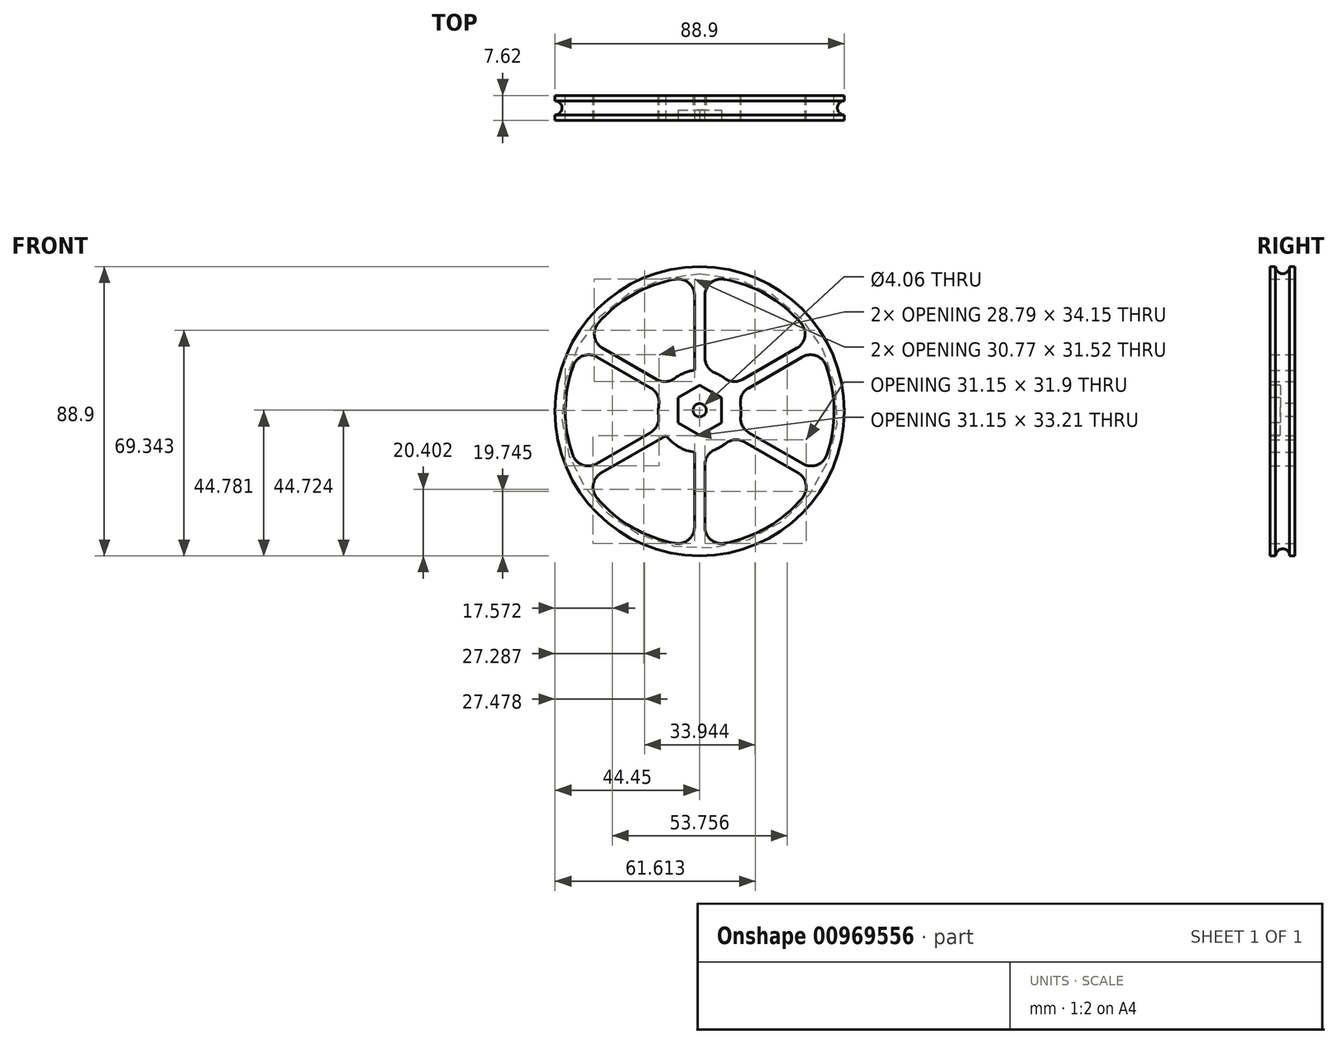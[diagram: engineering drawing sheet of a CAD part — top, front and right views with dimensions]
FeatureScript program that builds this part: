
annotation { "Feature Type Name" : "Feature", "Feature Type Description" : "" }
export const myFeature = defineFeature(function(context is Context, id is Id, definition is map)
    precondition{}
    {
        {
            var Q0;
            Q0=qCreatedBy(makeId("Top.planeOp"),FACE);
            var sketch = newSketch(context, id + "F0", { "sketchPlane" : qUnion([Q0])});
            skLineSegment(sketch, "E0", {"start": v(0, 0) * mm, "end": v(0, 3.81) * mm});
            skLineSegment(sketch, "E1", {"start": v(0, 0) * mm, "end": v(0, -3.81) * mm});
            skLineSegment(sketch, "E2", {"start": v(0, 3.81) * mm, "end": v(44.45, 3.81) * mm});
            skLineSegment(sketch, "E3", {"start": v(0, -3.81) * mm, "end": v(44.45, -3.81) * mm});
            skLineSegment(sketch, "E4", {"start": v(44.45, 3.8) * mm, "end": v(44.45, 2.16) * mm});
            skLineSegment(sketch, "E5", {"start": v(44.45, -3.8) * mm, "end": v(44.45, -2.16) * mm});
            skLineSegment(sketch, "E6", {"start": v(44.45, 2.16) * mm, "end": v(44.45, -2.16) * mm});
            skCircle(sketch, "E7", {"center": v(44.45, 0) * mm, "radius": 2.16 * mm});
            skLineSegment(sketch, "E8", {"start": v(44.45, 2.16) * mm, "end": v(0, 2.16) * mm});
            skLineSegment(sketch, "E9", {"start": v(44.45, -2.16) * mm, "end": v(0, -2.16) * mm});
            skPoint(sketch, "E9.endSnap0", {"position": v(0, -1.9) * mm});
            skSolve(sketch);
        }
        {
            var Q0;
            {var subQ0=sQuery(id+"F0.wireOp",EDGE,"E2");Q0=makeQuery(id+"F0.imprint","IMPRINT",FACE,{"disambiguationData":[TD([[makeQuery(id+"F0.imprint","IMPRINT",EDGE,{"derivedFrom":subQ0}),-1.0]])]});}
            var Q1;
            {var subQ0=sQuery(id+"F0.wireOp",EDGE,"E3");Q1=makeQuery(id+"F0.imprint","IMPRINT",FACE,{"disambiguationData":[TD([[makeQuery(id+"F0.imprint","IMPRINT",EDGE,{"derivedFrom":subQ0}),1.0]])]});}
            var Q2;
            {var subQ0=sQuery(id+"F0.wireOp",EDGE,"E8");Q2=makeQuery(id+"F0.imprint","IMPRINT",FACE,{"disambiguationData":[TD([[makeQuery(id+"F0.imprint","IMPRINT",EDGE,{"derivedFrom":subQ0}),1.0]])]});}
            var Q3;
            Q3 = qSketchRegion(id + "F2", true);
            var Q4;
            Q4=sQuery(id+"F0.wireOp",EDGE,"E1");
            revolve(context, id + "F1", {"surfaceOperationType" : NewSurfaceOperationType.NEW, "entities" : qUnion([Q0, Q1, Q2, Q3]), "axis" : qUnion([Q4]), "revolveType" : RevolveType.FULL});
        }
        {
            var Q0;
            Q0=makeQuery(id+"F1.opRevolve","SWEPT_FACE",FACE,{"disambiguationData":[OSD([sQuery(id+"F0.wireOp",EDGE,"E2")])]});
            var sketch = newSketch(context, id + "F2", { "sketchPlane" : qUnion([Q0])});
            skCircle(sketch, "E10", {"center": v(0, 0) * mm, "radius": 41.28 * mm});
            skSolve(sketch);
        }
        {
            var Q0;
            Q0=makeQuery(id+"F2.imprint","IMPRINT",FACE,{"disambiguationData":[TD([[makeQuery(id+"F2.imprint","IMPRINT",EDGE,{"derivedFrom":sQuery(id+"F2.wireOp",EDGE,"E10")}),1.0]])]});
            var Q1;
            Q1=sQuery(id+"F2.wireOp",EDGE,"E10");
            extrude(context, id + "F3", {"entities" : qUnion([Q0]), "operationType" : NewBodyOperationType.REMOVE, "surfaceEntities" : qUnion([Q1]), "endBound" : BoundingType.THROUGH_ALL, "oppositeDirection" : true, "depth" : 25.4 * mm, "offsetDistance" : 25.4 * mm});
        }
        {
            var Q0;
            Q0=qCreatedBy(makeId("Front.planeOp"),FACE);
            var sketch = newSketch(context, id + "F4", { "sketchPlane" : qUnion([Q0])});
            skLineSegment(sketch, "E11.0", {"start": v(-6.64, 4.17) * mm, "end": v(0, 8) * mm});
            skLineSegment(sketch, "E11.1", {"start": v(0, 8) * mm, "end": v(6.64, 4.17) * mm});
            skLineSegment(sketch, "E11.2", {"start": v(6.64, 4.17) * mm, "end": v(6.64, -3.5) * mm});
            skLineSegment(sketch, "E11.3", {"start": v(6.64, -3.5) * mm, "end": v(0, -7.34) * mm});
            skLineSegment(sketch, "E11.4", {"start": v(0, -7.34) * mm, "end": v(-6.64, -3.5) * mm});
            skLineSegment(sketch, "E11.5", {"start": v(-6.64, -3.5) * mm, "end": v(-6.64, 4.17) * mm});
            skCircle(sketch, "E12", {"center": v(0, 0) * mm, "radius": 12.7 * mm});
            skLineSegment(sketch, "E13", {"start": v(0, 8) * mm, "end": v(0, 9.82) * mm});
            skLineSegment(sketch, "E14", {"start": v(0, 9.82) * mm, "end": v(0, -7.34) * mm});
            skCircle(sketch, "E15", {"center": v(0, 0) * mm, "radius": 9.82 * mm});
            skLineSegment(sketch, "E16", {"start": v(0, -7.34) * mm, "end": v(0, 8) * mm});
            skLineSegment(sketch, "E17", {"start": v(6.64, 4.17) * mm, "end": v(-6.64, -3.5) * mm});
            skLineSegment(sketch, "E18", {"start": v(6.64, -3.5) * mm, "end": v(8.64, -4.66) * mm});
            skLineSegment(sketch, "E19", {"start": v(6.64, -3.5) * mm, "end": v(-6.64, 4.17) * mm});
            skLineSegment(sketch, "E20", {"start": v(0, 8) * mm, "end": v(0, 41.58) * mm});
            skCircle(sketch, "E21", {"center": v(0, 0) * mm, "radius": 41.58 * mm});
            skLineSegment(sketch, "E22", {"start": v(6.64, 4.17) * mm, "end": v(35.87, 21.04) * mm});
            skLineSegment(sketch, "E23", {"start": v(8.64, -4.66) * mm, "end": v(36.16, -20.54) * mm});
            skLineSegment(sketch, "E24", {"start": v(0, -7.34) * mm, "end": v(0, -41.58) * mm});
            skLineSegment(sketch, "E25", {"start": v(-6.64, -3.5) * mm, "end": v(-36.16, -20.54) * mm});
            skLineSegment(sketch, "E26", {"start": v(-6.64, 4.17) * mm, "end": v(-35.87, 21.04) * mm});
            skLineSegment(sketch, "E27", {"start": v(1.59, 12.6) * mm, "end": v(1.59, 41.55) * mm});
            skLineSegment(sketch, "E28", {"start": v(-1.59, 12.6) * mm, "end": v(-1.59, 41.55) * mm});
            skLineSegment(sketch, "E29", {"start": v(-9.94, 7.9) * mm, "end": v(-35.04, 22.4) * mm});
            skLineSegment(sketch, "E30", {"start": v(-11.6, 5.19) * mm, "end": v(-36.65, 19.66) * mm});
            skLineSegment(sketch, "E31", {"start": v(-11.82, -4.66) * mm, "end": v(-36.91, -19.15) * mm});
            skLineSegment(sketch, "E32", {"start": v(-10.3, -7.44) * mm, "end": v(-35.34, -21.9) * mm});
            skLineSegment(sketch, "E33", {"start": v(10.3, -7.44) * mm, "end": v(35.34, -21.9) * mm});
            skLineSegment(sketch, "E34", {"start": v(11.82, -4.66) * mm, "end": v(36.91, -19.15) * mm});
            skLineSegment(sketch, "E35", {"start": v(11.6, 5.19) * mm, "end": v(36.65, 19.66) * mm});
            skLineSegment(sketch, "E36", {"start": v(9.94, 7.9) * mm, "end": v(35.04, 22.4) * mm});
            skLineSegment(sketch, "E37", {"start": v(1.59, -12.6) * mm, "end": v(1.59, -41.55) * mm});
            skPoint(sketch, "E37.startSnap0", {"position": v(22.4, -12.6) * mm});
            skLineSegment(sketch, "E38", {"start": v(-1.59, -12.6) * mm, "end": v(-1.59, -41.55) * mm});
            skSolve(sketch);
        }
        {
            var Q0;
            {var subQ0=sQuery(id+"F4.wireOp",EDGE,"E36");Q0=makeQuery(id+"F4.imprint","IMPRINT",FACE,{"disambiguationData":[TD([[makeQuery(id+"F4.imprint","IMPRINT",EDGE,{"derivedFrom":subQ0}),-1.0]])]});}
            var Q1;
            {var subQ0=sQuery(id+"F4.wireOp",EDGE,"E35");Q1=makeQuery(id+"F4.imprint","IMPRINT",FACE,{"disambiguationData":[TD([[makeQuery(id+"F4.imprint","IMPRINT",EDGE,{"derivedFrom":subQ0}),1.0]])]});}
            var Q2;
            {var subQ0=sQuery(id+"F4.wireOp",EDGE,"E27");Q2=makeQuery(id+"F4.imprint","IMPRINT",FACE,{"disambiguationData":[TD([[makeQuery(id+"F4.imprint","IMPRINT",EDGE,{"derivedFrom":subQ0}),1.0]])]});}
            var Q3;
            {var subQ0=sQuery(id+"F4.wireOp",EDGE,"E28");Q3=makeQuery(id+"F4.imprint","IMPRINT",FACE,{"disambiguationData":[TD([[makeQuery(id+"F4.imprint","IMPRINT",EDGE,{"derivedFrom":subQ0}),-1.0]])]});}
            var Q4;
            {var subQ0=sQuery(id+"F4.wireOp",EDGE,"E29");Q4=makeQuery(id+"F4.imprint","IMPRINT",FACE,{"disambiguationData":[TD([[makeQuery(id+"F4.imprint","IMPRINT",EDGE,{"derivedFrom":subQ0}),1.0]])]});}
            var Q5;
            {var subQ0=sQuery(id+"F4.wireOp",EDGE,"E30");Q5=makeQuery(id+"F4.imprint","IMPRINT",FACE,{"disambiguationData":[TD([[makeQuery(id+"F4.imprint","IMPRINT",EDGE,{"derivedFrom":subQ0}),-1.0]])]});}
            var Q6;
            {var subQ0=sQuery(id+"F4.wireOp",EDGE,"E31");Q6=makeQuery(id+"F4.imprint","IMPRINT",FACE,{"disambiguationData":[TD([[makeQuery(id+"F4.imprint","IMPRINT",EDGE,{"derivedFrom":subQ0}),1.0]])]});}
            var Q7;
            {var subQ0=sQuery(id+"F4.wireOp",EDGE,"E32");Q7=makeQuery(id+"F4.imprint","IMPRINT",FACE,{"disambiguationData":[TD([[makeQuery(id+"F4.imprint","IMPRINT",EDGE,{"derivedFrom":subQ0}),-1.0]])]});}
            var Q8;
            {var subQ0=sQuery(id+"F4.wireOp",EDGE,"E33");Q8=makeQuery(id+"F4.imprint","IMPRINT",FACE,{"disambiguationData":[TD([[makeQuery(id+"F4.imprint","IMPRINT",EDGE,{"derivedFrom":subQ0}),1.0]])]});}
            var Q9;
            {var subQ0=sQuery(id+"F4.wireOp",EDGE,"E34");Q9=makeQuery(id+"F4.imprint","IMPRINT",FACE,{"disambiguationData":[TD([[makeQuery(id+"F4.imprint","IMPRINT",EDGE,{"derivedFrom":subQ0}),-1.0]])]});}
            var Q10;
            {var subQ0=sQuery(id+"F4.wireOp",EDGE,"E37");Q10=makeQuery(id+"F4.imprint","IMPRINT",FACE,{"disambiguationData":[TD([[makeQuery(id+"F4.imprint","IMPRINT",EDGE,{"derivedFrom":subQ0}),-1.0]])]});}
            var Q11;
            {var subQ0=sQuery(id+"F4.wireOp",EDGE,"E38");Q11=makeQuery(id+"F4.imprint","IMPRINT",FACE,{"disambiguationData":[TD([[makeQuery(id+"F4.imprint","IMPRINT",EDGE,{"derivedFrom":subQ0}),1.0]])]});}
            extrude(context, id + "F5", {"entities" : qUnion([Q0, Q1, Q2, Q3, Q4, Q5, Q6, Q7, Q8, Q9, Q10, Q11]), "operationType" : NewBodyOperationType.ADD, "endBound" : BoundingType.SYMMETRIC, "depth" : 7.62 * mm, "offsetDistance" : 25.4 * mm});
        }
        {
            var Q0;
            {var subQ5=sQuery(id+"F4.wireOp",EDGE,"E12");var subQ7=makeQuery(id+"F4.imprint","INTERSECT",VERTEX,{"derivedFrom":[subQ5,sQuery(id+"F4.wireOp",EDGE,"E35")]});Q0=makeQuery(id+"F4.imprint","IMPRINT",FACE,{"disambiguationData":[TD([[makeQuery(id+"F4.imprint","IMPRINT",EDGE,{"disambiguationData":[TD([[subQ7,-1.0]])],"derivedFrom":subQ5}),1.0]])]});}
            var Q1;
            {var subQ0=sQuery(id+"F4.wireOp",EDGE,"E12");var subQ4=makeQuery(id+"F4.imprint","INTERSECT",VERTEX,{"derivedFrom":[subQ0,sQuery(id+"F4.wireOp",EDGE,"E36")]});Q1=makeQuery(id+"F4.imprint","IMPRINT",FACE,{"disambiguationData":[TD([[makeQuery(id+"F4.imprint","IMPRINT",EDGE,{"disambiguationData":[TD([[subQ4,1.0]])],"derivedFrom":subQ0}),1.0]])]});}
            var Q2;
            {var subQ4=sQuery(id+"F4.wireOp",EDGE,"E12");var subQ8=makeQuery(id+"F4.imprint","INTERSECT",VERTEX,{"derivedFrom":[subQ4,sQuery(id+"F4.wireOp",EDGE,"E28")]});Q2=makeQuery(id+"F4.imprint","IMPRINT",FACE,{"disambiguationData":[TD([[makeQuery(id+"F4.imprint","IMPRINT",EDGE,{"disambiguationData":[TD([[subQ8,1.0]])],"derivedFrom":subQ4}),1.0]])]});}
            var Q3;
            {var subQ5=sQuery(id+"F4.wireOp",EDGE,"E12");var subQ8=makeQuery(id+"F4.imprint","INTERSECT",VERTEX,{"derivedFrom":[subQ5,sQuery(id+"F4.wireOp",EDGE,"E30")]});Q3=makeQuery(id+"F4.imprint","IMPRINT",FACE,{"disambiguationData":[TD([[makeQuery(id+"F4.imprint","IMPRINT",EDGE,{"disambiguationData":[TD([[subQ8,1.0]])],"derivedFrom":subQ5}),1.0]])]});}
            var Q4;
            {var subQ0=sQuery(id+"F4.wireOp",EDGE,"E12");var subQ9=makeQuery(id+"F4.imprint","INTERSECT",VERTEX,{"derivedFrom":[subQ0,sQuery(id+"F4.wireOp",EDGE,"E32")]});Q4=makeQuery(id+"F4.imprint","IMPRINT",FACE,{"disambiguationData":[TD([[makeQuery(id+"F4.imprint","IMPRINT",EDGE,{"disambiguationData":[TD([[subQ9,1.0]])],"derivedFrom":subQ0}),1.0]])]});}
            var Q5;
            {var subQ0=sQuery(id+"F4.wireOp",EDGE,"E12");var subQ4=makeQuery(id+"F4.imprint","INTERSECT",VERTEX,{"derivedFrom":[subQ0,sQuery(id+"F4.wireOp",EDGE,"E37")]});Q5=makeQuery(id+"F4.imprint","IMPRINT",FACE,{"disambiguationData":[TD([[makeQuery(id+"F4.imprint","IMPRINT",EDGE,{"disambiguationData":[TD([[subQ4,1.0]])],"derivedFrom":subQ0}),1.0]])]});}
            var Q6;
            {var subQ0=sQuery(id+"F4.wireOp",EDGE,"E11.2");Q6=makeQuery(id+"F4.imprint","IMPRINT",FACE,{"disambiguationData":[TD([[makeQuery(id+"F4.imprint","IMPRINT",EDGE,{"derivedFrom":subQ0}),1.0]])]});}
            var Q7;
            {var subQ0=sQuery(id+"F4.wireOp",EDGE,"E11.3");Q7=makeQuery(id+"F4.imprint","IMPRINT",FACE,{"disambiguationData":[TD([[makeQuery(id+"F4.imprint","IMPRINT",EDGE,{"derivedFrom":subQ0}),1.0]])]});}
            var Q8;
            {var subQ0=sQuery(id+"F4.wireOp",EDGE,"E11.4");Q8=makeQuery(id+"F4.imprint","IMPRINT",FACE,{"disambiguationData":[TD([[makeQuery(id+"F4.imprint","IMPRINT",EDGE,{"derivedFrom":subQ0}),1.0]])]});}
            var Q9;
            {var subQ0=sQuery(id+"F4.wireOp",EDGE,"E11.5");Q9=makeQuery(id+"F4.imprint","IMPRINT",FACE,{"disambiguationData":[TD([[makeQuery(id+"F4.imprint","IMPRINT",EDGE,{"derivedFrom":subQ0}),1.0]])]});}
            var Q10;
            {var subQ0=sQuery(id+"F4.wireOp",EDGE,"E11.0");Q10=makeQuery(id+"F4.imprint","IMPRINT",FACE,{"disambiguationData":[TD([[makeQuery(id+"F4.imprint","IMPRINT",EDGE,{"derivedFrom":subQ0}),1.0]])]});}
            var Q11;
            {var subQ0=sQuery(id+"F4.wireOp",EDGE,"F7P9rnZc-xmLm-aryr-64I1-wp8JT27DvNvk");Q11=makeQuery(id+"F4.imprint","IMPRINT",FACE,{"disambiguationData":[TD([[makeQuery(id+"F4.imprint","IMPRINT",EDGE,{"derivedFrom":subQ0}),1.0]])]});}
            var Q12;
            {var subQ0=sQuery(id+"F4.wireOp",EDGE,"E11.1");Q12=makeQuery(id+"F4.imprint","IMPRINT",FACE,{"disambiguationData":[TD([[makeQuery(id+"F4.imprint","IMPRINT",EDGE,{"derivedFrom":subQ0}),1.0]])]});}
            extrude(context, id + "F6", {"entities" : qUnion([Q0, Q1, Q2, Q3, Q4, Q5, Q6, Q7, Q8, Q9, Q10, Q11, Q12]), "operationType" : NewBodyOperationType.ADD, "endBound" : BoundingType.SYMMETRIC, "depth" : 7.62 * mm, "offsetDistance" : 25.4 * mm});
        }
        {
            var Q0;
            {var subQ0=sQuery(id+"F4.wireOp",EDGE,"E11.4");Q0=makeQuery(id+"F4.imprint","IMPRINT",FACE,{"disambiguationData":[TD([[makeQuery(id+"F4.imprint","IMPRINT",EDGE,{"derivedFrom":subQ0}),-1.0]])]});}
            var Q1;
            {var subQ0=sQuery(id+"F4.wireOp",EDGE,"E11.5");Q1=makeQuery(id+"F4.imprint","IMPRINT",FACE,{"disambiguationData":[TD([[makeQuery(id+"F4.imprint","IMPRINT",EDGE,{"derivedFrom":subQ0}),-1.0]])]});}
            var Q2;
            {var subQ0=sQuery(id+"F4.wireOp",EDGE,"E11.0");Q2=makeQuery(id+"F4.imprint","IMPRINT",FACE,{"disambiguationData":[TD([[makeQuery(id+"F4.imprint","IMPRINT",EDGE,{"derivedFrom":subQ0}),-1.0]])]});}
            var Q3;
            {var subQ0=sQuery(id+"F4.wireOp",EDGE,"E11.1");Q3=makeQuery(id+"F4.imprint","IMPRINT",FACE,{"disambiguationData":[TD([[makeQuery(id+"F4.imprint","IMPRINT",EDGE,{"derivedFrom":subQ0}),-1.0]])]});}
            var Q4;
            {var subQ0=sQuery(id+"F4.wireOp",EDGE,"E11.2");Q4=makeQuery(id+"F4.imprint","IMPRINT",FACE,{"disambiguationData":[TD([[makeQuery(id+"F4.imprint","IMPRINT",EDGE,{"derivedFrom":subQ0}),-1.0]])]});}
            var Q5;
            {var subQ0=sQuery(id+"F4.wireOp",EDGE,"E11.3");Q5=makeQuery(id+"F4.imprint","IMPRINT",FACE,{"disambiguationData":[TD([[makeQuery(id+"F4.imprint","IMPRINT",EDGE,{"derivedFrom":subQ0}),-1.0]])]});}
            var Q6;
            Q6 = qSketchRegion(id + "F8", true);
            extrude(context, id + "F7", {"entities" : qUnion([Q0, Q1, Q2, Q3, Q4, Q5, Q6]), "operationType" : NewBodyOperationType.ADD, "endBound" : BoundingType.SYMMETRIC, "depth" : 7.62 * mm, "offsetDistance" : 25.4 * mm});
        }
        {
            var Q0;
            {var subQ0=sQuery(id+"F4.wireOp",EDGE,"E11.5");var subQ1=sQuery(id+"F4.wireOp",EDGE,"E11.4");var subQ2=sQuery(id+"F4.wireOp",EDGE,"E11.3");var subQ3=sQuery(id+"F4.wireOp",EDGE,"E11.2");var subQ4=sQuery(id+"F4.wireOp",EDGE,"E11.1");var subQ5=sQuery(id+"F4.wireOp",EDGE,"E11.0");Q0=makeQuery(id+"F7.boolean.opBoolean","MERGE",FACE,{"derivedFrom":[makeQuery(id+"F6.opExtrude","CAP_FACE",FACE,{"disambiguationData":[OSD([subQ5,subQ4,subQ3,subQ2,subQ1,subQ0,sQuery(id+"F4.wireOp",EDGE,"E12")])],"isStart":false}),makeQuery(id+"F7.opExtrude","CAP_FACE",FACE,{"disambiguationData":[OSD([subQ5,subQ4,subQ3,subQ2,subQ1,subQ0])],"isStart":false})]});}
            var sketch = newSketch(context, id + "F8", { "sketchPlane" : qUnion([Q0])});
            skLineSegment(sketch, "E39.1", {"start": v(-6.64, 4.17) * mm, "end": v(0, 8) * mm});
            skLineSegment(sketch, "E39.2", {"start": v(0, -7.34) * mm, "end": v(0, 8) * mm});
            skLineSegment(sketch, "E39.3", {"start": v(0, 8) * mm, "end": v(6.64, 4.17) * mm});
            skLineSegment(sketch, "E39.4", {"start": v(6.64, -3.5) * mm, "end": v(-6.64, 4.17) * mm});
            skLineSegment(sketch, "E39.5", {"start": v(-6.64, -3.5) * mm, "end": v(-6.64, 4.17) * mm});
            skLineSegment(sketch, "E39.6", {"start": v(0, -7.34) * mm, "end": v(-6.64, -3.5) * mm});
            skLineSegment(sketch, "E39.7", {"start": v(6.64, 4.17) * mm, "end": v(-6.64, -3.5) * mm});
            skLineSegment(sketch, "E39.8", {"start": v(6.64, 4.17) * mm, "end": v(6.64, -3.5) * mm});
            skLineSegment(sketch, "E39.9", {"start": v(6.64, -3.5) * mm, "end": v(0, -7.34) * mm});
            skPoint(sketch, "E39.10", {"position": v(6.64, 0.33) * mm});
            skCircle(sketch, "E40", {"center": v(9.99, -16.46) * mm, "radius": 1.14 * mm});
            skCircle(sketch, "E41", {"center": v(0, 0.33) * mm, "radius": 2.03 * mm});
            skSolve(sketch);
        }
        {
            var Q0;
            {var subQ0=sQuery(id+"F8.wireOp",EDGE,"E39.8");Q0=makeQuery(id+"F8.imprint","IMPRINT",FACE,{"disambiguationData":[TD([[makeQuery(id+"F8.imprint","IMPRINT",EDGE,{"derivedFrom":subQ0}),-1.0]])]});}
            var Q1;
            {var subQ0=sQuery(id+"F8.wireOp",EDGE,"E39.9");Q1=makeQuery(id+"F8.imprint","IMPRINT",FACE,{"disambiguationData":[TD([[makeQuery(id+"F8.imprint","IMPRINT",EDGE,{"derivedFrom":subQ0}),-1.0]])]});}
            var Q2;
            {var subQ0=sQuery(id+"F8.wireOp",EDGE,"E39.6");Q2=makeQuery(id+"F8.imprint","IMPRINT",FACE,{"disambiguationData":[TD([[makeQuery(id+"F8.imprint","IMPRINT",EDGE,{"derivedFrom":subQ0}),-1.0]])]});}
            var Q3;
            {var subQ0=sQuery(id+"F8.wireOp",EDGE,"E39.5");Q3=makeQuery(id+"F8.imprint","IMPRINT",FACE,{"disambiguationData":[TD([[makeQuery(id+"F8.imprint","IMPRINT",EDGE,{"derivedFrom":subQ0}),-1.0]])]});}
            var Q4;
            {var subQ0=sQuery(id+"F8.wireOp",EDGE,"E39.1");Q4=makeQuery(id+"F8.imprint","IMPRINT",FACE,{"disambiguationData":[TD([[makeQuery(id+"F8.imprint","IMPRINT",EDGE,{"derivedFrom":subQ0}),-1.0]])]});}
            var Q5;
            {var subQ0=sQuery(id+"F8.wireOp",EDGE,"E39.3");Q5=makeQuery(id+"F8.imprint","IMPRINT",FACE,{"disambiguationData":[TD([[makeQuery(id+"F8.imprint","IMPRINT",EDGE,{"derivedFrom":subQ0}),-1.0]])]});}
            extrude(context, id + "F9", {"entities" : qUnion([Q0, Q1, Q2, Q3, Q4, Q5]), "operationType" : NewBodyOperationType.REMOVE, "oppositeDirection" : true, "depth" : 3.17 * mm, "offsetDistance" : 25.4 * mm});
        }
        {
            var Q0;
            {var subQ0=sQuery(id+"F8.wireOp",EDGE,"E41");var subQ1=sQuery(id+"F8.wireOp",EDGE,"E39.2");var subQ2=makeQuery(id+"F8.imprint","INTERSECT",VERTEX,{"disambiguationData":[OD(0.0)],"derivedFrom":[subQ1,subQ0]});Q0=makeQuery(id+"F8.imprint","IMPRINT",FACE,{"disambiguationData":[TD([[makeQuery(id+"F8.imprint","IMPRINT",EDGE,{"disambiguationData":[TD([[subQ2,1.0]])],"derivedFrom":subQ0}),1.0]])]});}
            var Q1;
            {var subQ0=sQuery(id+"F8.wireOp",EDGE,"E41");var subQ1=sQuery(id+"F8.wireOp",EDGE,"E39.4");var subQ2=makeQuery(id+"F8.imprint","INTERSECT",VERTEX,{"disambiguationData":[OD(1.0)],"derivedFrom":[subQ1,subQ0]});Q1=makeQuery(id+"F8.imprint","IMPRINT",FACE,{"disambiguationData":[TD([[makeQuery(id+"F8.imprint","IMPRINT",EDGE,{"disambiguationData":[TD([[subQ2,-1.0]])],"derivedFrom":subQ0}),1.0]])]});}
            var Q2;
            {var subQ0=sQuery(id+"F8.wireOp",EDGE,"E41");var subQ1=sQuery(id+"F8.wireOp",EDGE,"E39.2");var subQ2=makeQuery(id+"F8.imprint","INTERSECT",VERTEX,{"disambiguationData":[OD(1.0)],"derivedFrom":[subQ1,subQ0]});Q2=makeQuery(id+"F8.imprint","IMPRINT",FACE,{"disambiguationData":[TD([[makeQuery(id+"F8.imprint","IMPRINT",EDGE,{"disambiguationData":[TD([[subQ2,-1.0]])],"derivedFrom":subQ0}),1.0]])]});}
            var Q3;
            {var subQ0=sQuery(id+"F8.wireOp",EDGE,"E41");var subQ1=sQuery(id+"F8.wireOp",EDGE,"E39.2");var subQ2=makeQuery(id+"F8.imprint","INTERSECT",VERTEX,{"disambiguationData":[OD(1.0)],"derivedFrom":[subQ1,subQ0]});Q3=makeQuery(id+"F8.imprint","IMPRINT",FACE,{"disambiguationData":[TD([[makeQuery(id+"F8.imprint","IMPRINT",EDGE,{"disambiguationData":[TD([[subQ2,1.0]])],"derivedFrom":subQ0}),1.0]])]});}
            var Q4;
            {var subQ0=sQuery(id+"F8.wireOp",EDGE,"E41");var subQ1=sQuery(id+"F8.wireOp",EDGE,"E39.4");var subQ2=makeQuery(id+"F8.imprint","INTERSECT",VERTEX,{"disambiguationData":[OD(0.0)],"derivedFrom":[subQ1,subQ0]});Q4=makeQuery(id+"F8.imprint","IMPRINT",FACE,{"disambiguationData":[TD([[makeQuery(id+"F8.imprint","IMPRINT",EDGE,{"disambiguationData":[TD([[subQ2,-1.0]])],"derivedFrom":subQ0}),1.0]])]});}
            var Q5;
            {var subQ0=sQuery(id+"F8.wireOp",EDGE,"E41");var subQ1=sQuery(id+"F8.wireOp",EDGE,"E39.2");var subQ2=makeQuery(id+"F8.imprint","INTERSECT",VERTEX,{"disambiguationData":[OD(0.0)],"derivedFrom":[subQ1,subQ0]});Q5=makeQuery(id+"F8.imprint","IMPRINT",FACE,{"disambiguationData":[TD([[makeQuery(id+"F8.imprint","IMPRINT",EDGE,{"disambiguationData":[TD([[subQ2,-1.0]])],"derivedFrom":subQ0}),1.0]])]});}
            extrude(context, id + "F10", {"entities" : qUnion([Q0, Q1, Q2, Q3, Q4, Q5]), "operationType" : NewBodyOperationType.REMOVE, "endBound" : BoundingType.THROUGH_ALL, "oppositeDirection" : true, "depth" : 25.4 * mm, "offsetDistance" : 25.4 * mm});
        }
        {
            var Q0;
            Q0=makeQuery(id+"F5.boolean.opBoolean","INTERSECT",EDGE,{"derivedFrom":[makeQuery(id+"F3.boolean.opBoolean","COPY",FACE,{"derivedFrom":makeQuery(id+"F3.opExtrude","SWEPT_FACE",FACE,{"disambiguationData":[OSD([sQuery(id+"F2.wireOp",EDGE,"E10")])]})}),makeQuery(id+"F5.opExtrude","CAP_FACE",FACE,{"disambiguationData":[OSD([sQuery(id+"F4.wireOp",EDGE,"E12"),sQuery(id+"F4.wireOp",EDGE,"E21"),sQuery(id+"F4.wireOp",EDGE,"E37"),sQuery(id+"F4.wireOp",EDGE,"E38")])],"isStart":false})]});
            var Q1;
            Q1=makeQuery(id+"F5.boolean.opBoolean","INTERSECT",EDGE,{"derivedFrom":[makeQuery(id+"F3.boolean.opBoolean","COPY",FACE,{"derivedFrom":makeQuery(id+"F3.opExtrude","SWEPT_FACE",FACE,{"disambiguationData":[OSD([sQuery(id+"F2.wireOp",EDGE,"E10")])]})}),makeQuery(id+"F5.opExtrude","SWEPT_FACE",FACE,{"disambiguationData":[OSD([sQuery(id+"F4.wireOp",EDGE,"E37")])]})]});
            var Q2;
            Q2=makeQuery(id+"F5.boolean.opBoolean","INTERSECT",EDGE,{"derivedFrom":[makeQuery(id+"F3.boolean.opBoolean","COPY",FACE,{"derivedFrom":makeQuery(id+"F3.opExtrude","SWEPT_FACE",FACE,{"disambiguationData":[OSD([sQuery(id+"F2.wireOp",EDGE,"E10")])]})}),makeQuery(id+"F5.opExtrude","SWEPT_FACE",FACE,{"disambiguationData":[OSD([sQuery(id+"F4.wireOp",EDGE,"E38")])]})]});
            var Q3;
            Q3=makeQuery(id+"F5.boolean.opBoolean","INTERSECT",EDGE,{"derivedFrom":[makeQuery(id+"F3.boolean.opBoolean","COPY",FACE,{"derivedFrom":makeQuery(id+"F3.opExtrude","SWEPT_FACE",FACE,{"disambiguationData":[OSD([sQuery(id+"F2.wireOp",EDGE,"E10")])]})}),makeQuery(id+"F5.opExtrude","SWEPT_FACE",FACE,{"disambiguationData":[OSD([sQuery(id+"F4.wireOp",EDGE,"E34")])]})]});
            var Q4;
            Q4=makeQuery(id+"F5.boolean.opBoolean","INTERSECT",EDGE,{"derivedFrom":[makeQuery(id+"F3.boolean.opBoolean","COPY",FACE,{"derivedFrom":makeQuery(id+"F3.opExtrude","SWEPT_FACE",FACE,{"disambiguationData":[OSD([sQuery(id+"F2.wireOp",EDGE,"E10")])]})}),makeQuery(id+"F5.opExtrude","CAP_FACE",FACE,{"disambiguationData":[OSD([sQuery(id+"F4.wireOp",EDGE,"E12"),sQuery(id+"F4.wireOp",EDGE,"E21"),sQuery(id+"F4.wireOp",EDGE,"E33"),sQuery(id+"F4.wireOp",EDGE,"E34")])],"isStart":false})]});
            var Q5;
            Q5=makeQuery(id+"F5.boolean.opBoolean","INTERSECT",EDGE,{"derivedFrom":[makeQuery(id+"F3.boolean.opBoolean","COPY",FACE,{"derivedFrom":makeQuery(id+"F3.opExtrude","SWEPT_FACE",FACE,{"disambiguationData":[OSD([sQuery(id+"F2.wireOp",EDGE,"E10")])]})}),makeQuery(id+"F5.opExtrude","CAP_FACE",FACE,{"disambiguationData":[OSD([sQuery(id+"F4.wireOp",EDGE,"E12"),sQuery(id+"F4.wireOp",EDGE,"E21"),sQuery(id+"F4.wireOp",EDGE,"E37"),sQuery(id+"F4.wireOp",EDGE,"E38")])],"isStart":true})]});
            var Q6;
            Q6=makeQuery(id+"F5.boolean.opBoolean","INTERSECT",EDGE,{"derivedFrom":[makeQuery(id+"F3.boolean.opBoolean","COPY",FACE,{"derivedFrom":makeQuery(id+"F3.opExtrude","SWEPT_FACE",FACE,{"disambiguationData":[OSD([sQuery(id+"F2.wireOp",EDGE,"E10")])]})}),makeQuery(id+"F5.opExtrude","CAP_FACE",FACE,{"disambiguationData":[OSD([sQuery(id+"F4.wireOp",EDGE,"E12"),sQuery(id+"F4.wireOp",EDGE,"E21"),sQuery(id+"F4.wireOp",EDGE,"E33"),sQuery(id+"F4.wireOp",EDGE,"E34")])],"isStart":true})]});
            var Q7;
            Q7=makeQuery(id+"F5.boolean.opBoolean","INTERSECT",EDGE,{"derivedFrom":[makeQuery(id+"F3.boolean.opBoolean","COPY",FACE,{"derivedFrom":makeQuery(id+"F3.opExtrude","SWEPT_FACE",FACE,{"disambiguationData":[OSD([sQuery(id+"F2.wireOp",EDGE,"E10")])]})}),makeQuery(id+"F5.opExtrude","SWEPT_FACE",FACE,{"disambiguationData":[OSD([sQuery(id+"F4.wireOp",EDGE,"E33")])]})]});
            var Q8;
            Q8=makeQuery(id+"F5.boolean.opBoolean","INTERSECT",EDGE,{"derivedFrom":[makeQuery(id+"F3.boolean.opBoolean","COPY",FACE,{"derivedFrom":makeQuery(id+"F3.opExtrude","SWEPT_FACE",FACE,{"disambiguationData":[OSD([sQuery(id+"F2.wireOp",EDGE,"E10")])]})}),makeQuery(id+"F5.opExtrude","CAP_FACE",FACE,{"disambiguationData":[OSD([sQuery(id+"F4.wireOp",EDGE,"E12"),sQuery(id+"F4.wireOp",EDGE,"E21"),sQuery(id+"F4.wireOp",EDGE,"E35"),sQuery(id+"F4.wireOp",EDGE,"E36")])],"isStart":true})]});
            var Q9;
            Q9=makeQuery(id+"F5.boolean.opBoolean","INTERSECT",EDGE,{"derivedFrom":[makeQuery(id+"F3.boolean.opBoolean","COPY",FACE,{"derivedFrom":makeQuery(id+"F3.opExtrude","SWEPT_FACE",FACE,{"disambiguationData":[OSD([sQuery(id+"F2.wireOp",EDGE,"E10")])]})}),makeQuery(id+"F5.opExtrude","SWEPT_FACE",FACE,{"disambiguationData":[OSD([sQuery(id+"F4.wireOp",EDGE,"E36")])]})]});
            var Q10;
            Q10=makeQuery(id+"F5.boolean.opBoolean","INTERSECT",EDGE,{"derivedFrom":[makeQuery(id+"F3.boolean.opBoolean","COPY",FACE,{"derivedFrom":makeQuery(id+"F3.opExtrude","SWEPT_FACE",FACE,{"disambiguationData":[OSD([sQuery(id+"F2.wireOp",EDGE,"E10")])]})}),makeQuery(id+"F5.opExtrude","CAP_FACE",FACE,{"disambiguationData":[OSD([sQuery(id+"F4.wireOp",EDGE,"E12"),sQuery(id+"F4.wireOp",EDGE,"E21"),sQuery(id+"F4.wireOp",EDGE,"E35"),sQuery(id+"F4.wireOp",EDGE,"E36")])],"isStart":false})]});
            var Q11;
            Q11=makeQuery(id+"F5.boolean.opBoolean","INTERSECT",EDGE,{"derivedFrom":[makeQuery(id+"F3.boolean.opBoolean","COPY",FACE,{"derivedFrom":makeQuery(id+"F3.opExtrude","SWEPT_FACE",FACE,{"disambiguationData":[OSD([sQuery(id+"F2.wireOp",EDGE,"E10")])]})}),makeQuery(id+"F5.opExtrude","SWEPT_FACE",FACE,{"disambiguationData":[OSD([sQuery(id+"F4.wireOp",EDGE,"E35")])]})]});
            var Q12;
            Q12=makeQuery(id+"F5.boolean.opBoolean","INTERSECT",EDGE,{"derivedFrom":[makeQuery(id+"F3.boolean.opBoolean","COPY",FACE,{"derivedFrom":makeQuery(id+"F3.opExtrude","SWEPT_FACE",FACE,{"disambiguationData":[OSD([sQuery(id+"F2.wireOp",EDGE,"E10")])]})}),makeQuery(id+"F5.opExtrude","SWEPT_FACE",FACE,{"disambiguationData":[OSD([sQuery(id+"F4.wireOp",EDGE,"E28")])]})]});
            var Q13;
            Q13=makeQuery(id+"F5.boolean.opBoolean","INTERSECT",EDGE,{"derivedFrom":[makeQuery(id+"F3.boolean.opBoolean","COPY",FACE,{"derivedFrom":makeQuery(id+"F3.opExtrude","SWEPT_FACE",FACE,{"disambiguationData":[OSD([sQuery(id+"F2.wireOp",EDGE,"E10")])]})}),makeQuery(id+"F5.opExtrude","CAP_FACE",FACE,{"disambiguationData":[OSD([sQuery(id+"F4.wireOp",EDGE,"E12"),sQuery(id+"F4.wireOp",EDGE,"E21"),sQuery(id+"F4.wireOp",EDGE,"E27"),sQuery(id+"F4.wireOp",EDGE,"E28")])],"isStart":false})]});
            fillet(context, id + "F11", {"entities" : qUnion([Q0, Q1, Q2, Q3, Q4, Q5, Q6, Q7, Q8, Q9, Q10, Q11, Q12, Q13]), "radius" : 5.08 * mm, "tangentPropagation" : true, "allowEdgeOverflow" : false});
        }
        {
            var Q0;
            Q0=makeQuery(id+"F5.boolean.opBoolean","INTERSECT",EDGE,{"derivedFrom":[makeQuery(id+"F3.boolean.opBoolean","COPY",FACE,{"derivedFrom":makeQuery(id+"F3.opExtrude","SWEPT_FACE",FACE,{"disambiguationData":[OSD([sQuery(id+"F2.wireOp",EDGE,"E10")])]})}),makeQuery(id+"F5.opExtrude","CAP_FACE",FACE,{"disambiguationData":[OSD([sQuery(id+"F4.wireOp",EDGE,"E12"),sQuery(id+"F4.wireOp",EDGE,"E21"),sQuery(id+"F4.wireOp",EDGE,"E27"),sQuery(id+"F4.wireOp",EDGE,"E28")])],"isStart":true})]});
            var Q1;
            Q1=makeQuery(id+"F5.boolean.opBoolean","INTERSECT",EDGE,{"derivedFrom":[makeQuery(id+"F3.boolean.opBoolean","COPY",FACE,{"derivedFrom":makeQuery(id+"F3.opExtrude","SWEPT_FACE",FACE,{"disambiguationData":[OSD([sQuery(id+"F2.wireOp",EDGE,"E10")])]})}),makeQuery(id+"F5.opExtrude","SWEPT_FACE",FACE,{"disambiguationData":[OSD([sQuery(id+"F4.wireOp",EDGE,"E27")])]})]});
            var Q2;
            Q2=makeQuery(id+"F5.boolean.opBoolean","INTERSECT",EDGE,{"derivedFrom":[makeQuery(id+"F3.boolean.opBoolean","COPY",FACE,{"derivedFrom":makeQuery(id+"F3.opExtrude","SWEPT_FACE",FACE,{"disambiguationData":[OSD([sQuery(id+"F2.wireOp",EDGE,"E10")])]})}),makeQuery(id+"F5.opExtrude","CAP_FACE",FACE,{"disambiguationData":[OSD([sQuery(id+"F4.wireOp",EDGE,"E12"),sQuery(id+"F4.wireOp",EDGE,"E21"),sQuery(id+"F4.wireOp",EDGE,"E31"),sQuery(id+"F4.wireOp",EDGE,"E32")])],"isStart":false})]});
            var Q3;
            Q3=makeQuery(id+"F5.boolean.opBoolean","INTERSECT",EDGE,{"derivedFrom":[makeQuery(id+"F3.boolean.opBoolean","COPY",FACE,{"derivedFrom":makeQuery(id+"F3.opExtrude","SWEPT_FACE",FACE,{"disambiguationData":[OSD([sQuery(id+"F2.wireOp",EDGE,"E10")])]})}),makeQuery(id+"F5.opExtrude","SWEPT_FACE",FACE,{"disambiguationData":[OSD([sQuery(id+"F4.wireOp",EDGE,"E32")])]})]});
            var Q4;
            Q4=makeQuery(id+"F5.boolean.opBoolean","INTERSECT",EDGE,{"derivedFrom":[makeQuery(id+"F3.boolean.opBoolean","COPY",FACE,{"derivedFrom":makeQuery(id+"F3.opExtrude","SWEPT_FACE",FACE,{"disambiguationData":[OSD([sQuery(id+"F2.wireOp",EDGE,"E10")])]})}),makeQuery(id+"F5.opExtrude","CAP_FACE",FACE,{"disambiguationData":[OSD([sQuery(id+"F4.wireOp",EDGE,"E12"),sQuery(id+"F4.wireOp",EDGE,"E21"),sQuery(id+"F4.wireOp",EDGE,"E29"),sQuery(id+"F4.wireOp",EDGE,"E30")])],"isStart":false})]});
            var Q5;
            Q5=makeQuery(id+"F5.boolean.opBoolean","INTERSECT",EDGE,{"derivedFrom":[makeQuery(id+"F3.boolean.opBoolean","COPY",FACE,{"derivedFrom":makeQuery(id+"F3.opExtrude","SWEPT_FACE",FACE,{"disambiguationData":[OSD([sQuery(id+"F2.wireOp",EDGE,"E10")])]})}),makeQuery(id+"F5.opExtrude","SWEPT_FACE",FACE,{"disambiguationData":[OSD([sQuery(id+"F4.wireOp",EDGE,"E29")])]})]});
            var Q6;
            Q6=makeQuery(id+"F5.boolean.opBoolean","INTERSECT",EDGE,{"derivedFrom":[makeQuery(id+"F3.boolean.opBoolean","COPY",FACE,{"derivedFrom":makeQuery(id+"F3.opExtrude","SWEPT_FACE",FACE,{"disambiguationData":[OSD([sQuery(id+"F2.wireOp",EDGE,"E10")])]})}),makeQuery(id+"F5.opExtrude","SWEPT_FACE",FACE,{"disambiguationData":[OSD([sQuery(id+"F4.wireOp",EDGE,"E30")])]})]});
            var Q7;
            Q7=makeQuery(id+"F5.boolean.opBoolean","INTERSECT",EDGE,{"derivedFrom":[makeQuery(id+"F3.boolean.opBoolean","COPY",FACE,{"derivedFrom":makeQuery(id+"F3.opExtrude","SWEPT_FACE",FACE,{"disambiguationData":[OSD([sQuery(id+"F2.wireOp",EDGE,"E10")])]})}),makeQuery(id+"F5.opExtrude","CAP_FACE",FACE,{"disambiguationData":[OSD([sQuery(id+"F4.wireOp",EDGE,"E12"),sQuery(id+"F4.wireOp",EDGE,"E21"),sQuery(id+"F4.wireOp",EDGE,"E29"),sQuery(id+"F4.wireOp",EDGE,"E30")])],"isStart":true})]});
            fillet(context, id + "F12", {"entities" : qUnion([Q0, Q1, Q2, Q3, Q4, Q5, Q6, Q7]), "radius" : 5.08 * mm, "tangentPropagation" : true, "allowEdgeOverflow" : false});
        }
        {
            var Q0;
            Q0=makeQuery(id+"F5.boolean.opBoolean","INTERSECT",EDGE,{"derivedFrom":[makeQuery(id+"F3.boolean.opBoolean","COPY",FACE,{"derivedFrom":makeQuery(id+"F3.opExtrude","SWEPT_FACE",FACE,{"disambiguationData":[OSD([sQuery(id+"F2.wireOp",EDGE,"E10")])]})}),makeQuery(id+"F5.opExtrude","SWEPT_FACE",FACE,{"disambiguationData":[OSD([sQuery(id+"F4.wireOp",EDGE,"E31")])]})]});
            var Q1;
            Q1=makeQuery(id+"F5.boolean.opBoolean","INTERSECT",EDGE,{"derivedFrom":[makeQuery(id+"F3.boolean.opBoolean","COPY",FACE,{"derivedFrom":makeQuery(id+"F3.opExtrude","SWEPT_FACE",FACE,{"disambiguationData":[OSD([sQuery(id+"F2.wireOp",EDGE,"E10")])]})}),makeQuery(id+"F5.opExtrude","CAP_FACE",FACE,{"disambiguationData":[OSD([sQuery(id+"F4.wireOp",EDGE,"E12"),sQuery(id+"F4.wireOp",EDGE,"E21"),sQuery(id+"F4.wireOp",EDGE,"E31"),sQuery(id+"F4.wireOp",EDGE,"E32")])],"isStart":true})]});
            var Q2;
            {var subQ0=makeQuery(id+"F5.opExtrude","CAP_FACE",FACE,{"disambiguationData":[OSD([sQuery(id+"F4.wireOp",EDGE,"E12"),sQuery(id+"F4.wireOp",EDGE,"E21"),sQuery(id+"F4.wireOp",EDGE,"E31"),sQuery(id+"F4.wireOp",EDGE,"E32")])],"isStart":false});Q2=makeQuery(id+"F12.opFillet","BLEND_EDGE",EDGE,{"disambiguationData":[OD(1.0)],"blendedFrom":[makeQuery(id+"F5.boolean.opBoolean","INTERSECT",EDGE,{"derivedFrom":[makeQuery(id+"F3.boolean.opBoolean","COPY",FACE,{"derivedFrom":makeQuery(id+"F3.opExtrude","SWEPT_FACE",FACE,{"disambiguationData":[OSD([sQuery(id+"F2.wireOp",EDGE,"E10")])]})}),subQ0]}),subQ0],"blendedInto":[subQ0]});}
            var Q3;
            Q3=makeQuery(id+"F5.opExtrude","SWEPT_EDGE",EDGE,{"disambiguationData":[OSD([sQuery(id+"F4.wireOp",EDGE,"E12"),sQuery(id+"F4.wireOp",EDGE,"E31")])]});
            var Q4;
            {var subQ0=sQuery(id+"F4.wireOp",EDGE,"E12");Q4=makeQuery(id+"F5.opExtrude","CAP_EDGE",EDGE,{"disambiguationData":[OSD([subQ0]),TDD([makeQuery(id+"F4.imprint","IMPRINT",EDGE,{"disambiguationData":[TD([[makeQuery(id+"F4.imprint","INTERSECT",VERTEX,{"derivedFrom":[subQ0,sQuery(id+"F4.wireOp",EDGE,"E31")]}),-1.0]])],"derivedFrom":subQ0}),makeQuery(id+"F4.imprint","IMPRINT",EDGE,{"disambiguationData":[TD([[makeQuery(id+"F4.imprint","INTERSECT",VERTEX,{"derivedFrom":[subQ0,sQuery(id+"F4.wireOp",EDGE,"E32")]}),1.0]])],"derivedFrom":subQ0})])],"isStart":true});}
            var Q5;
            Q5=makeQuery(id+"F5.opExtrude","SWEPT_EDGE",EDGE,{"disambiguationData":[OSD([sQuery(id+"F4.wireOp",EDGE,"E12"),sQuery(id+"F4.wireOp",EDGE,"E32")])]});
            var Q6;
            {var subQ0=sQuery(id+"F4.wireOp",EDGE,"E12");Q6=makeQuery(id+"F5.opExtrude","CAP_EDGE",EDGE,{"disambiguationData":[OSD([subQ0]),TDD([makeQuery(id+"F4.imprint","IMPRINT",EDGE,{"disambiguationData":[TD([[makeQuery(id+"F4.imprint","INTERSECT",VERTEX,{"derivedFrom":[subQ0,sQuery(id+"F4.wireOp",EDGE,"E31")]}),-1.0]])],"derivedFrom":subQ0}),makeQuery(id+"F4.imprint","IMPRINT",EDGE,{"disambiguationData":[TD([[makeQuery(id+"F4.imprint","INTERSECT",VERTEX,{"derivedFrom":[subQ0,sQuery(id+"F4.wireOp",EDGE,"E32")]}),1.0]])],"derivedFrom":subQ0})])],"isStart":false});}
            var Q7;
            {var subQ0=sQuery(id+"F4.wireOp",EDGE,"E12");Q7=makeQuery(id+"F5.opExtrude","CAP_EDGE",EDGE,{"disambiguationData":[OSD([subQ0]),TDD([makeQuery(id+"F4.imprint","IMPRINT",EDGE,{"disambiguationData":[TD([[makeQuery(id+"F4.imprint","INTERSECT",VERTEX,{"derivedFrom":[subQ0,sQuery(id+"F4.wireOp",EDGE,"E38")]}),-1.0]])],"derivedFrom":subQ0}),makeQuery(id+"F4.imprint","IMPRINT",EDGE,{"disambiguationData":[TD([[makeQuery(id+"F4.imprint","INTERSECT",VERTEX,{"derivedFrom":[subQ0,sQuery(id+"F4.wireOp",EDGE,"E37")]}),1.0]])],"derivedFrom":subQ0})])],"isStart":false});}
            var Q8;
            {var subQ0=sQuery(id+"F4.wireOp",EDGE,"E12");Q8=makeQuery(id+"F5.opExtrude","CAP_EDGE",EDGE,{"disambiguationData":[OSD([subQ0]),TDD([makeQuery(id+"F4.imprint","IMPRINT",EDGE,{"disambiguationData":[TD([[makeQuery(id+"F4.imprint","INTERSECT",VERTEX,{"derivedFrom":[subQ0,sQuery(id+"F4.wireOp",EDGE,"E33")]}),-1.0]])],"derivedFrom":subQ0}),makeQuery(id+"F4.imprint","IMPRINT",EDGE,{"disambiguationData":[TD([[makeQuery(id+"F4.imprint","INTERSECT",VERTEX,{"derivedFrom":[subQ0,sQuery(id+"F4.wireOp",EDGE,"E34")]}),1.0]])],"derivedFrom":subQ0})])],"isStart":false});}
            var Q9;
            Q9=makeQuery(id+"F5.opExtrude","SWEPT_EDGE",EDGE,{"disambiguationData":[OSD([sQuery(id+"F4.wireOp",EDGE,"E12"),sQuery(id+"F4.wireOp",EDGE,"E37")])]});
            var Q10;
            Q10=makeQuery(id+"F5.opExtrude","SWEPT_EDGE",EDGE,{"disambiguationData":[OSD([sQuery(id+"F4.wireOp",EDGE,"E12"),sQuery(id+"F4.wireOp",EDGE,"E33")])]});
            var Q11;
            Q11=makeQuery(id+"F5.opExtrude","SWEPT_EDGE",EDGE,{"disambiguationData":[OSD([sQuery(id+"F4.wireOp",EDGE,"E12"),sQuery(id+"F4.wireOp",EDGE,"E34")])]});
            var Q12;
            {var subQ0=sQuery(id+"F4.wireOp",EDGE,"E12");Q12=makeQuery(id+"F5.opExtrude","CAP_EDGE",EDGE,{"disambiguationData":[OSD([subQ0]),TDD([makeQuery(id+"F4.imprint","IMPRINT",EDGE,{"disambiguationData":[TD([[makeQuery(id+"F4.imprint","INTERSECT",VERTEX,{"derivedFrom":[subQ0,sQuery(id+"F4.wireOp",EDGE,"E33")]}),-1.0]])],"derivedFrom":subQ0}),makeQuery(id+"F4.imprint","IMPRINT",EDGE,{"disambiguationData":[TD([[makeQuery(id+"F4.imprint","INTERSECT",VERTEX,{"derivedFrom":[subQ0,sQuery(id+"F4.wireOp",EDGE,"E34")]}),1.0]])],"derivedFrom":subQ0})])],"isStart":true});}
            var Q13;
            {var subQ0=sQuery(id+"F4.wireOp",EDGE,"E12");Q13=makeQuery(id+"F5.opExtrude","CAP_EDGE",EDGE,{"disambiguationData":[OSD([subQ0]),TDD([makeQuery(id+"F4.imprint","IMPRINT",EDGE,{"disambiguationData":[TD([[makeQuery(id+"F4.imprint","INTERSECT",VERTEX,{"derivedFrom":[subQ0,sQuery(id+"F4.wireOp",EDGE,"E35")]}),-1.0]])],"derivedFrom":subQ0}),makeQuery(id+"F4.imprint","IMPRINT",EDGE,{"disambiguationData":[TD([[makeQuery(id+"F4.imprint","INTERSECT",VERTEX,{"derivedFrom":[subQ0,sQuery(id+"F4.wireOp",EDGE,"E36")]}),1.0]])],"derivedFrom":subQ0})])],"isStart":true});}
            var Q14;
            Q14=makeQuery(id+"F5.opExtrude","SWEPT_EDGE",EDGE,{"disambiguationData":[OSD([sQuery(id+"F4.wireOp",EDGE,"E12"),sQuery(id+"F4.wireOp",EDGE,"E36")])]});
            var Q15;
            Q15=makeQuery(id+"F5.opExtrude","SWEPT_EDGE",EDGE,{"disambiguationData":[OSD([sQuery(id+"F4.wireOp",EDGE,"E12"),sQuery(id+"F4.wireOp",EDGE,"E27")])]});
            var Q16;
            Q16=makeQuery(id+"F5.opExtrude","SWEPT_EDGE",EDGE,{"disambiguationData":[OSD([sQuery(id+"F4.wireOp",EDGE,"E12"),sQuery(id+"F4.wireOp",EDGE,"E29")])]});
            var Q17;
            Q17=makeQuery(id+"F5.opExtrude","SWEPT_EDGE",EDGE,{"disambiguationData":[OSD([sQuery(id+"F4.wireOp",EDGE,"E12"),sQuery(id+"F4.wireOp",EDGE,"E30")])]});
            var Q18;
            Q18=makeQuery(id+"F5.opExtrude","SWEPT_EDGE",EDGE,{"disambiguationData":[OSD([sQuery(id+"F4.wireOp",EDGE,"E12"),sQuery(id+"F4.wireOp",EDGE,"E38")])]});
            var Q19;
            {var subQ0=sQuery(id+"F4.wireOp",EDGE,"E12");Q19=makeQuery(id+"F5.opExtrude","CAP_EDGE",EDGE,{"disambiguationData":[OSD([subQ0]),TDD([makeQuery(id+"F4.imprint","IMPRINT",EDGE,{"disambiguationData":[TD([[makeQuery(id+"F4.imprint","INTERSECT",VERTEX,{"derivedFrom":[subQ0,sQuery(id+"F4.wireOp",EDGE,"E38")]}),-1.0]])],"derivedFrom":subQ0}),makeQuery(id+"F4.imprint","IMPRINT",EDGE,{"disambiguationData":[TD([[makeQuery(id+"F4.imprint","INTERSECT",VERTEX,{"derivedFrom":[subQ0,sQuery(id+"F4.wireOp",EDGE,"E37")]}),1.0]])],"derivedFrom":subQ0})])],"isStart":true});}
            var Q20;
            {var subQ0=sQuery(id+"F4.wireOp",EDGE,"E12");Q20=makeQuery(id+"F5.opExtrude","CAP_EDGE",EDGE,{"disambiguationData":[OSD([subQ0]),TDD([makeQuery(id+"F4.imprint","IMPRINT",EDGE,{"disambiguationData":[TD([[makeQuery(id+"F4.imprint","INTERSECT",VERTEX,{"derivedFrom":[subQ0,sQuery(id+"F4.wireOp",EDGE,"E29")]}),-1.0]])],"derivedFrom":subQ0}),makeQuery(id+"F4.imprint","IMPRINT",EDGE,{"disambiguationData":[TD([[makeQuery(id+"F4.imprint","INTERSECT",VERTEX,{"derivedFrom":[subQ0,sQuery(id+"F4.wireOp",EDGE,"E30")]}),1.0]])],"derivedFrom":subQ0})])],"isStart":true});}
            var Q21;
            Q21=makeQuery(id+"F5.opExtrude","SWEPT_EDGE",EDGE,{"disambiguationData":[OSD([sQuery(id+"F4.wireOp",EDGE,"E12"),sQuery(id+"F4.wireOp",EDGE,"E35")])]});
            var Q22;
            {var subQ0=sQuery(id+"F4.wireOp",EDGE,"E12");Q22=makeQuery(id+"F5.opExtrude","CAP_EDGE",EDGE,{"disambiguationData":[OSD([subQ0]),TDD([makeQuery(id+"F4.imprint","IMPRINT",EDGE,{"disambiguationData":[TD([[makeQuery(id+"F4.imprint","INTERSECT",VERTEX,{"derivedFrom":[subQ0,sQuery(id+"F4.wireOp",EDGE,"E35")]}),-1.0]])],"derivedFrom":subQ0}),makeQuery(id+"F4.imprint","IMPRINT",EDGE,{"disambiguationData":[TD([[makeQuery(id+"F4.imprint","INTERSECT",VERTEX,{"derivedFrom":[subQ0,sQuery(id+"F4.wireOp",EDGE,"E36")]}),1.0]])],"derivedFrom":subQ0})])],"isStart":false});}
            fillet(context, id + "F13", {"entities" : qUnion([Q0, Q1, Q2, Q3, Q4, Q5, Q6, Q7, Q8, Q9, Q10, Q11, Q12, Q13, Q14, Q15, Q16, Q17, Q18, Q19, Q20, Q21, Q22]), "radius" : 5.08 * mm, "tangentPropagation" : true, "allowEdgeOverflow" : false});
        }
    });
